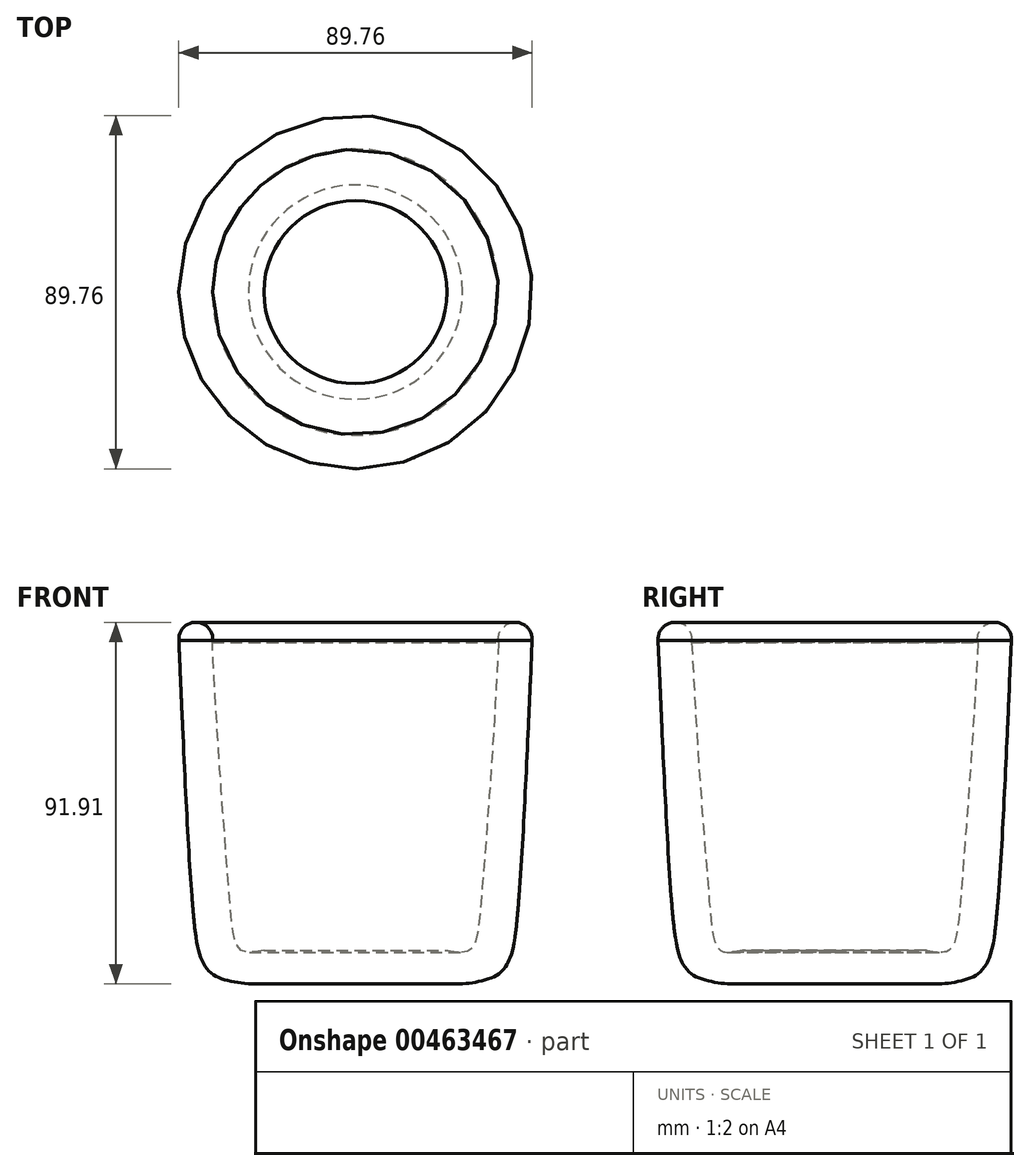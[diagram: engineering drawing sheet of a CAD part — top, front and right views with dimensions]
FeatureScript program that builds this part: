
annotation { "Feature Type Name" : "Feature", "Feature Type Description" : "" }
export const myFeature = defineFeature(function(context is Context, id is Id, definition is map)
    precondition{}
    {
        {
            var Q0;
            Q0=qCreatedBy(makeId("Front.planeOp"),FACE);
            var sketch = newSketch(context, id + "F0", { "sketchPlane" : qUnion([Q0])});
            skLineSegment(sketch, "E0", {"start": v(0, -55.59) * mm, "end": v(-27.22, -55.59) * mm});
            skFitSpline(sketch, "E1", {"points": [v(-27.22, -55.59) * mm, v(-36.96, -52.55) * mm, v(-41.22, -37.33) * mm, v(-44.87, 31.74) * mm], "startDerivative": vector(-53.98, 6.98) * mm, "endDerivative": vector(-6.33, 148.8) * mm});
            skLineSegment(sketch, "E2", {"start": v(0, -47.07) * mm, "end": v(-23.27, -47.07) * mm});
            skFitSpline(sketch, "E3", {"points": [v(-23.27, -47.07) * mm, v(-29.05, -47.07) * mm, v(-30.88, -43.42) * mm, v(-31.79, -35.8) * mm, v(-34.53, 0) * mm, v(-36.35, 31.13) * mm], "startDerivative": vector(-52.48, -9.27) * mm, "endDerivative": vector(-5.13, 97.15) * mm});
            skArc(sketch, "E4", {"start": v(-36.35, 31.13) * mm, "mid": v(-40.27, 36.3) * mm, "end": v(-44.87, 31.74) * mm});
            skLineSegment(sketch, "E5", {"start": v(0, -55.59) * mm, "end": v(0, -47.07) * mm});
            skFitSpline(sketch, "E6", {"points": [v(-44.42, 21.09) * mm, v(-56.74, 25.35) * mm, v(-67.09, 21.1) * mm, v(-73.78, 4.05) * mm, v(-72.56, -17.25) * mm, v(-67.4, -33.07) * mm, v(-58.87, -41.9) * mm, v(-52.48, -44.03) * mm, v(-40.5, -43.79) * mm], "startDerivative": vector(-101.48, 49.82) * mm, "endDerivative": vector(110.6, 6.83) * mm});
            skFitSpline(sketch, "E7", {"points": [v(-43.93, 9.85) * mm, v(-52.78, 17.14) * mm, v(-58.26, 17.44) * mm, v(-63.13, 15.31) * mm, v(-66.48, 9.53) * mm, v(-68.3, -4.47) * mm, v(-67.09, -17.25) * mm, v(-63.43, -29.12) * mm, v(-58.26, -35.8) * mm, v(-49.74, -38.85) * mm, v(-45.18, -38.24) * mm, v(-41.55, -33.33) * mm], "startDerivative": vector(-87.54, 86.56) * mm, "endDerivative": vector(43.05, 77.03) * mm});
            skSolve(sketch);
        }
        {
            var Q0;
            {var subQ6=sQuery(id+"F0.wireOp",EDGE,"E0");Q0=makeQuery(id+"F0.imprint","IMPRINT",FACE,{"disambiguationData":[TD([[makeQuery(id+"F0.imprint","IMPRINT",EDGE,{"derivedFrom":subQ6}),-1.0]])]});}
            var Q1;
            Q1=sQuery(id+"F0.wireOp",EDGE,"E5");
            revolve(context, id + "F1", {"entities" : qUnion([Q0]), "axis" : qUnion([Q1]), "revolveType" : RevolveType.FULL});
        }
    });
